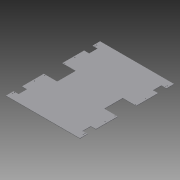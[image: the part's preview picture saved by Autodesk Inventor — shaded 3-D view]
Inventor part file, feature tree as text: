
AUTODESK INVENTOR PART (.ipt)
format: ipt  version: 2015 SP1 (Build 190203100, 203)  size: 203,264 bytes
history: native  units: in
note: dims shown in document units (in); Inventor stores cm internally (conversion verified against a paired STEP export)
features: sketch x3, hole x2, projected_geometry x2, extrude x1
ambient origin geometry x8: Origin, YZ Plane, XZ Plane, XY Plane, X Axis, Y Axis, Z Axis, Center Point
bodies: Solid1 (feature_tree)
feature tree (8):
  extrude  "Extrusion1"  Depth=28.0in
  hole  "Hole1"  [1 undecoded]
  hole  "Hole2"  [1 undecoded]
  sketch  "Sketch1"  dims[d0=22.0in d1=28.0in]
  sketch  "Sketch2"  dims[d2=4.0in d3=2.75in]
  projected_geometry  "Projected Loop1"
  sketch  "Sketch3"  dims[d4=4.0in d5=2.75in d6=4.0in d7=2.75in d8=4.0in d9=2.75in d10=2.25in d11=1.5in d12=2.5in d13=2.25in d14=1.5in d15=2.5in d16=2.25in d17=1.5in d18=2.5in d19=2.25in d20=1.5in d21=2.5in d22=0.125in d23=0.0in d24=0.5in d25=0.5in d26=2.0in d27=1.5in d28=0.5in d29=0.5in d30=1.5in d31=2.0in d32=2.0in d33=1.5in d34=1.5in d35=2.0in d36=0.5in d37=0.5in d38=0.5in d39=0.5in d40=0.25in d41=0.75in d42=0.375in d43=0.25in d44=0.5635in d45=1.0in d46=0.8108in d47=0.5in d48=0.5in d49=3.25in d50=0.25in d51=0.25in d52=3.25in d53=0.5in d54=0.5in d55=0.5in d56=0.5in d57=0.25in d58=3.25in d59=0.25in d60=0.5in d61=3.25in d62=0.5in d63=0.25in d64=0.75in d65=0.375in d66=0.25in d67=0.5635in d68=1.0in d69=0.8108in]
  projected_geometry  "Projected Loop2"
note: 2 required parameter values undecoded (feature->parameter linkage not recoverable at this tier; creation-order binding heuristic only, values carry confidence <= 0.55)
